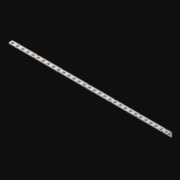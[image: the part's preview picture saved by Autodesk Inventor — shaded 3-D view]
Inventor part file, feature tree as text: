
AUTODESK INVENTOR PART (.ipt)
format: ipt  version: 2021 (Build 250183000, 183)  size: 837,632 bytes
history: native  units: in
note: dims shown in document units (in); Inventor stores cm internally (conversion verified against a paired STEP export)
features: extrude x63, other x62, sketch x3, pattern_linear x1, sheet_metal_op x1
ambient origin geometry x8: Origin, YZ Plane, XZ Plane, XY Plane, X Axis, Y Axis, Z Axis, Center Point
bodies: Solid1 (feature_tree)
feature tree (130):
  pattern_linear  "Rectangular Pattern1"  Spacing1=0.063in  [1 undecoded]
  extrude  "Extrusion1"  Depth=0.5in
  sketch  "Sketch1"  dims[d0=0.182in]
  other  "Srf1"
  sketch  "Sketch2"  dims[d1=0.063in d2=0.0in]
  other  "Srf2"
  other  "Srf3"
  other  "Srf5"
  other  "Srf7"
  other  "Srf9"
  other  "Srf11"
  other  "Srf13"
  other  "Srf15"
  other  "Srf17"
  other  "Srf19"
  other  "Srf21"
  other  "Srf23"
  other  "Srf25"
  other  "Srf27"
  other  "Srf29"
  other  "Srf31"
  other  "Srf33"
  other  "Srf35"
  other  "Srf37"
  other  "Srf39"
  other  "Srf41"
  other  "Srf43"
  other  "Srf45"
  other  "Srf47"
  other  "Srf49"
  other  "Srf51"
  other  "Srf53"
  other  "Srf55"
  other  "Srf57"
  other  "Srf59"
  other  "Srf61"
  other  "Srf4"
  other  "Srf6"
  other  "Srf8"
  other  "Srf10"
  other  "Srf12"
  other  "Srf14"
  other  "Srf16"
  other  "Srf18"
  other  "Srf20"
  other  "Srf22"
  other  "Srf24"
  other  "Srf26"
  other  "Srf28"
  other  "Srf30"
  other  "Srf32"
  other  "Srf34"
  other  "Srf36"
  other  "Srf38"
  other  "Srf40"
  other  "Srf42"
  other  "Srf44"
  other  "Srf46"
  other  "Srf48"
  other  "Srf50"
  other  "Srf52"
  other  "Srf54"
  other  "Srf56"
  other  "Srf58"
  other  "Srf60"
  other  "Srf62"
  sketch  "Sketch3"  dims[d3=0.182in d4=0.063in d5=0.0in d8=0.5in d9=2.0in d10=0.0in]
  sheet_metal_op  "Fold1"
  extrude  "ExtrusionSrf1"  Depth=0.5in TaperAngle=0.0deg
  extrude  "ExtrusionSrf2"  [1 undecoded]
  extrude  "ExtrusionSrf3"  [1 undecoded]
  extrude  "ExtrusionSrf4"  [1 undecoded]
  extrude  "ExtrusionSrf5"  [1 undecoded]
  extrude  "ExtrusionSrf6"  [1 undecoded]
  extrude  "ExtrusionSrf7"  [1 undecoded]
  extrude  "ExtrusionSrf8"  [1 undecoded]
  extrude  "ExtrusionSrf9"  [1 undecoded]
  extrude  "ExtrusionSrf10"  [1 undecoded]
  extrude  "ExtrusionSrf11"  [1 undecoded]
  extrude  "ExtrusionSrf12"  [1 undecoded]
  extrude  "ExtrusionSrf13"  [1 undecoded]
  extrude  "ExtrusionSrf14"  [1 undecoded]
  extrude  "ExtrusionSrf15"  [1 undecoded]
  extrude  "ExtrusionSrf16"  [1 undecoded]
  extrude  "ExtrusionSrf17"  [1 undecoded]
  extrude  "ExtrusionSrf18"  [1 undecoded]
  extrude  "ExtrusionSrf19"  [1 undecoded]
  extrude  "ExtrusionSrf20"  [1 undecoded]
  extrude  "ExtrusionSrf21"  [1 undecoded]
  extrude  "ExtrusionSrf22"  [1 undecoded]
  extrude  "ExtrusionSrf23"  [1 undecoded]
  extrude  "ExtrusionSrf24"  [1 undecoded]
  extrude  "ExtrusionSrf25"  [1 undecoded]
  extrude  "ExtrusionSrf26"  [1 undecoded]
  extrude  "ExtrusionSrf27"  [1 undecoded]
  extrude  "ExtrusionSrf28"  [1 undecoded]
  extrude  "ExtrusionSrf29"  [1 undecoded]
  extrude  "ExtrusionSrf30"  [1 undecoded]
  extrude  "ExtrusionSrf31"  [1 undecoded]
  extrude  "ExtrusionSrf32"  [1 undecoded]
  extrude  "ExtrusionSrf37"  [1 undecoded]
  extrude  "ExtrusionSrf38"  [1 undecoded]
  extrude  "ExtrusionSrf39"  [1 undecoded]
  extrude  "ExtrusionSrf40"  [1 undecoded]
  extrude  "ExtrusionSrf41"  [1 undecoded]
  extrude  "ExtrusionSrf42"  [1 undecoded]
  extrude  "ExtrusionSrf43"  [1 undecoded]
  extrude  "ExtrusionSrf44"  [1 undecoded]
  extrude  "ExtrusionSrf45"  [1 undecoded]
  extrude  "ExtrusionSrf46"  [1 undecoded]
  extrude  "ExtrusionSrf47"  [1 undecoded]
  extrude  "ExtrusionSrf48"  [1 undecoded]
  extrude  "ExtrusionSrf49"  [1 undecoded]
  extrude  "ExtrusionSrf50"  [1 undecoded]
  extrude  "ExtrusionSrf51"  [1 undecoded]
  extrude  "ExtrusionSrf52"  [1 undecoded]
  extrude  "ExtrusionSrf53"  [1 undecoded]
  extrude  "ExtrusionSrf54"  [1 undecoded]
  extrude  "ExtrusionSrf55"  [1 undecoded]
  extrude  "ExtrusionSrf56"  [1 undecoded]
  extrude  "ExtrusionSrf57"  [1 undecoded]
  extrude  "ExtrusionSrf58"  [1 undecoded]
  extrude  "ExtrusionSrf59"  [1 undecoded]
  extrude  "ExtrusionSrf60"  [1 undecoded]
  extrude  "ExtrusionSrf61"  [1 undecoded]
  extrude  "ExtrusionSrf62"  [1 undecoded]
  extrude  "ExtrusionSrf63"  [1 undecoded]
  extrude  "ExtrusionSrf64"  [1 undecoded]
  extrude  "ExtrusionSrf65"  [1 undecoded]
  extrude  "ExtrusionSrf66"  [1 undecoded]
note: 62 required parameter values undecoded (feature->parameter linkage not recoverable at this tier; creation-order binding heuristic only, values carry confidence <= 0.55)
